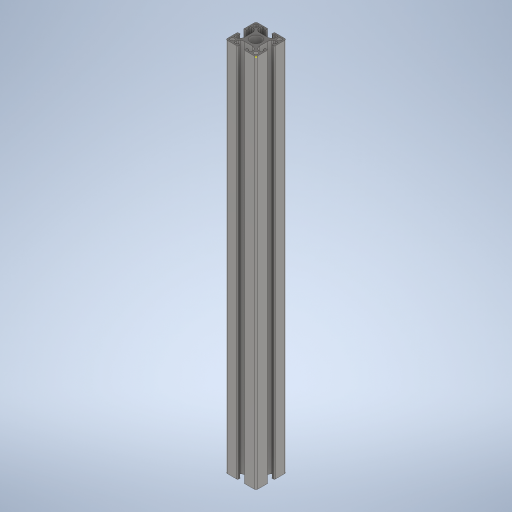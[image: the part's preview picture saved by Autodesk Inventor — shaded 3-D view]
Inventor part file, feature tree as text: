
AUTODESK INVENTOR PART (.ipt)
format: ipt  version: 2023 (Build 270158000, 158)  size: 488,448 bytes
history: native  units: mm
features: fillet x4, sketch x3, other x2, extrude x2
ambient origin geometry x8: Origin, YZ Plane, XZ Plane, XY Plane, X Axis, Y Axis, Z Axis, Center Point
bodies: Body1 (feature_tree)
feature tree (11):
  other  "Sólido1"
  extrude  "Extrusão1"  Depth=40.0mm
  sketch  "Esboço3"  dims[d18=2.0mm d19=15.0mm]
  fillet  "Arredondamento1"  Radius=3.81mm
  fillet  "Arredondamento2"  Radius=22.0mm
  fillet  "Arredondamento3"  Radius=20.0mm
  fillet  "Arredondamento4"  Radius=3.81mm
  extrude  "Extrusão2"  Depth=2.0mm
  sketch  "Esboço1"  dims[d11=15.905mm d12=40.0mm d13=3.81mm d14=22.0mm d15=20.0mm d17=3.81mm]
  sketch  "Esboço4"  dims[d20=494.0mm d21=0.0mm d22=2.0mm d23=1.0mm d24=3.0mm d25=6.0mm d26=14.0mm d27=0.0mm d28=0.0mm d29=40.0mm d30=5.0mm d31=5.0mm d32=5.0mm d33=5.0mm d34=31.0mm d35=4.5mm d36=31.0mm d37=4.5mm d38=31.0mm d39=31.0mm d40=4.5mm d41=4.5mm d42=0.0mm d43=0.0mm]
  other  "Projetar arestas de corte1"
